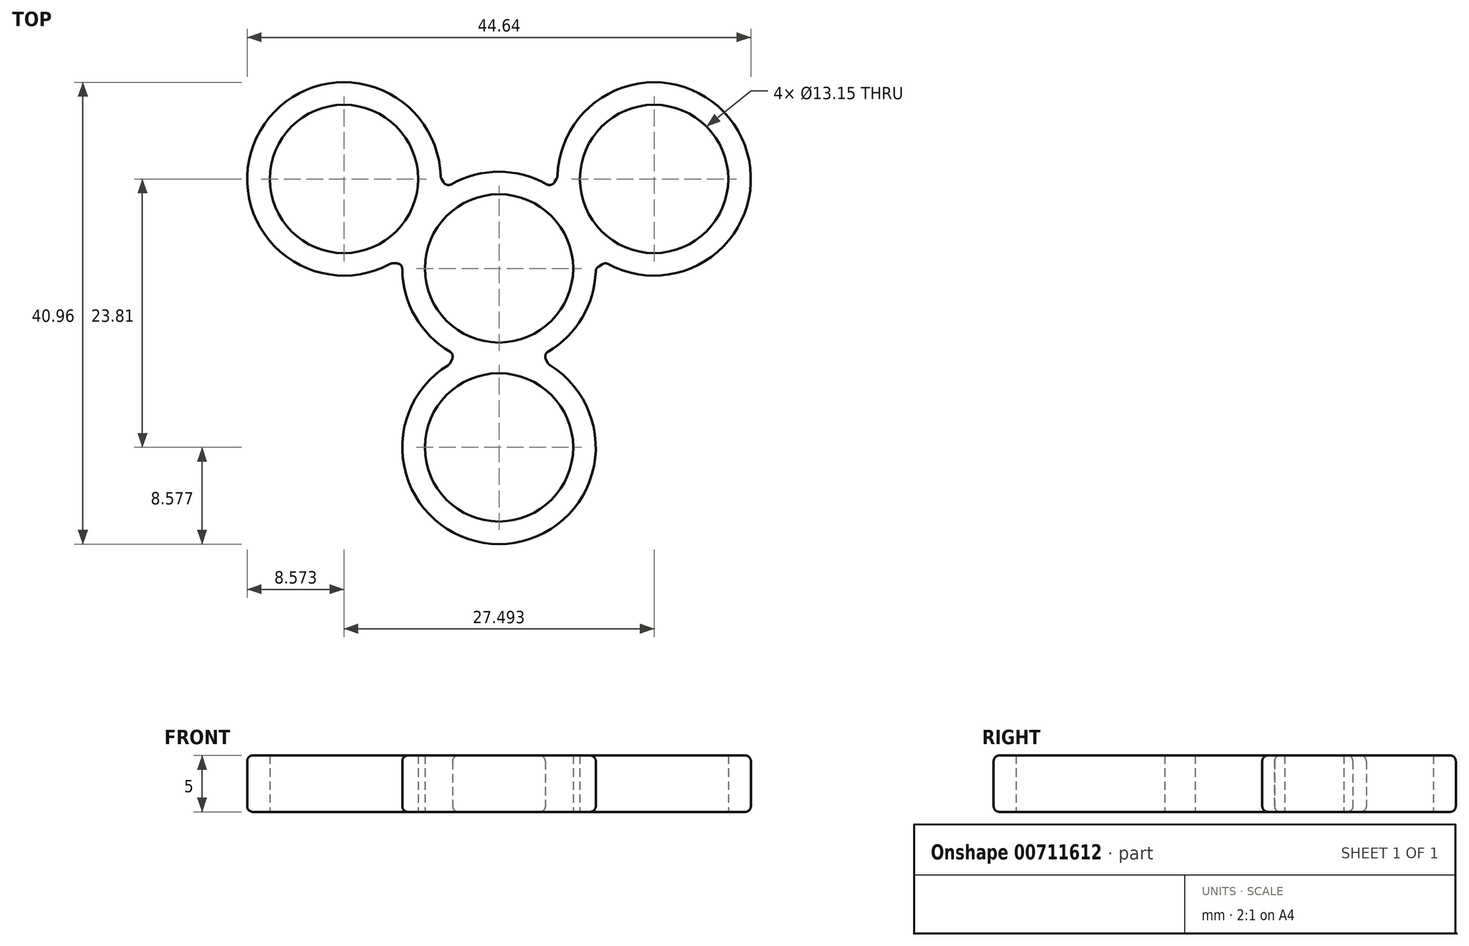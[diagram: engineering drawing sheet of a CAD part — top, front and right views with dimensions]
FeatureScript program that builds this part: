
annotation { "Feature Type Name" : "Feature", "Feature Type Description" : "" }
export const myFeature = defineFeature(function(context is Context, id is Id, definition is map)
    precondition{}
    {
        {
            assignVariable(context, id + "F0", {"name" : "bearing_thickness", "anyValue" : 5});
        }
        {
            var Q0;
            Q0=qCreatedBy(makeId("Top.planeOp"),FACE);
            var sketch = newSketch(context, id + "F1", { "sketchPlane" : qUnion([Q0])});
            skCircle(sketch, "E0", {"center": v(-13.75, 7.94) * mm, "radius": 6.57 * mm});
            skCircle(sketch, "E1", {"center": v(13.75, 7.94) * mm, "radius": 6.58 * mm});
            skCircle(sketch, "E2", {"center": v(0, -15.87) * mm, "radius": 6.58 * mm});
            skCircle(sketch, "E3", {"center": v(0, 0) * mm, "radius": 6.58 * mm});
            skLineSegment(sketch, "E4", {"start": v(-13.75, 7.94) * mm, "end": v(13.75, 7.94) * mm, "construction": true});
            skLineSegment(sketch, "E5", {"start": v(-13.75, 7.94) * mm, "end": v(0, -15.87) * mm, "construction": true});
            skLineSegment(sketch, "E6", {"start": v(13.75, 7.94) * mm, "end": v(0, -15.87) * mm, "construction": true});
            skLineSegment(sketch, "E7", {"start": v(0, 0) * mm, "end": v(-13.75, 7.94) * mm, "construction": true});
            skLineSegment(sketch, "E8", {"start": v(0, 0) * mm, "end": v(13.75, 7.94) * mm, "construction": true});
            skLineSegment(sketch, "E9", {"start": v(0, 0) * mm, "end": v(0, -15.87) * mm, "construction": true});
            skArc(sketch, "E10", {"start": v(-5.17, 8.06) * mm, "mid": v(-21.17, 12.22) * mm, "end": v(-9.56, 0.45) * mm});
            skArc(sketch, "E11", {"start": v(5.17, 8.06) * mm, "mid": v(21.21, 12.15) * mm, "end": v(9.42, 0.53) * mm});
            skArc(sketch, "E12", {"start": v(-4.4, -8.5) * mm, "mid": v(0, -24.45) * mm, "end": v(4.4, -8.5) * mm});
            skCircle(sketch, "E13", {"center": v(0, 0) * mm, "radius": 8.57 * mm});
            skLineSegment(sketch, "E14", {"start": v(-5.17, 8.06) * mm, "end": v(-4.63, 7.22) * mm});
            skLineSegment(sketch, "E15", {"start": v(-9.56, 0.45) * mm, "end": v(-8.56, 0.45) * mm});
            skLineSegment(sketch, "E16", {"start": v(5.17, 8.06) * mm, "end": v(4.63, 7.22) * mm});
            skLineSegment(sketch, "E17", {"start": v(9.42, 0.53) * mm, "end": v(8.57, 0) * mm});
            skLineSegment(sketch, "E18", {"start": v(4.4, -8.5) * mm, "end": v(3.93, -7.62) * mm});
            skLineSegment(sketch, "E19", {"start": v(-4.4, -8.5) * mm, "end": v(-3.93, -7.62) * mm});
            skSolve(sketch);
        }
        {
            var Q0;
            Q0=makeQuery(id+"F1.imprint","IMPRINT",FACE,{"disambiguationData":[TD([[makeQuery(id+"F1.imprint","IMPRINT",EDGE,{"derivedFrom":sQuery(id+"F1.wireOp",EDGE,"E0")}),-1.0]])]});
            var Q1;
            Q1=makeQuery(id+"F1.imprint","IMPRINT",FACE,{"disambiguationData":[TD([[makeQuery(id+"F1.imprint","IMPRINT",EDGE,{"derivedFrom":sQuery(id+"F1.wireOp",EDGE,"E1")}),-1.0]])]});
            var Q2;
            Q2=makeQuery(id+"F1.imprint","IMPRINT",FACE,{"disambiguationData":[TD([[makeQuery(id+"F1.imprint","IMPRINT",EDGE,{"derivedFrom":sQuery(id+"F1.wireOp",EDGE,"E2")}),-1.0]])]});
            var Q3;
            Q3=makeQuery(id+"F1.imprint","IMPRINT",FACE,{"disambiguationData":[TD([[makeQuery(id+"F1.imprint","IMPRINT",EDGE,{"derivedFrom":sQuery(id+"F1.wireOp",EDGE,"E3")}),-1.0]])]});
            extrude(context, id + "F2", {"entities" : qUnion([Q0, Q1, Q2, Q3]), "depth" : (getVariable(context, 'bearing_thickness')) * mm, "offsetDistance" : 25 * mm});
        }
        {
            var Q0;
            Q0=makeQuery(id+"F2.opExtrude","SWEPT_FACE",FACE,{"disambiguationData":[OSD([sQuery(id+"F1.wireOp",EDGE,"E10")])]});
            var Q1;
            {var subQ0=sQuery(id+"F1.wireOp",EDGE,"E13");Q1=makeQuery(id+"F2.opExtrude","SWEPT_FACE",FACE,{"disambiguationData":[OSD([subQ0]),TDD([makeQuery(id+"F1.imprint","IMPRINT",EDGE,{"disambiguationData":[TD([[makeQuery(id+"F1.imprint","INTERSECT",VERTEX,{"derivedFrom":[subQ0,sQuery(id+"F1.wireOp",EDGE,"E15")]}),-1.0]])],"derivedFrom":subQ0})])]});}
            var Q2;
            Q2=makeQuery(id+"F2.opExtrude","SWEPT_FACE",FACE,{"disambiguationData":[OSD([sQuery(id+"F1.wireOp",EDGE,"E12")])]});
            var Q3;
            Q3=makeQuery(id+"F2.opExtrude","SWEPT_FACE",FACE,{"disambiguationData":[OSD([sQuery(id+"F1.wireOp",EDGE,"E15")])]});
            var Q4;
            Q4=makeQuery(id+"F2.opExtrude","SWEPT_FACE",FACE,{"disambiguationData":[OSD([sQuery(id+"F1.wireOp",EDGE,"E19")])]});
            var Q5;
            Q5=makeQuery(id+"F2.opExtrude","SWEPT_FACE",FACE,{"disambiguationData":[OSD([sQuery(id+"F1.wireOp",EDGE,"E18")])]});
            var Q6;
            {var subQ0=sQuery(id+"F1.wireOp",EDGE,"E13");Q6=makeQuery(id+"F2.opExtrude","SWEPT_FACE",FACE,{"disambiguationData":[OSD([subQ0]),TDD([makeQuery(id+"F1.imprint","IMPRINT",EDGE,{"disambiguationData":[TD([[makeQuery(id+"F1.imprint","INTERSECT",VERTEX,{"derivedFrom":[subQ0,sQuery(id+"F1.wireOp",EDGE,"E17")]}),1.0]])],"derivedFrom":subQ0})])]});}
            var Q7;
            Q7=makeQuery(id+"F2.opExtrude","SWEPT_FACE",FACE,{"disambiguationData":[OSD([sQuery(id+"F1.wireOp",EDGE,"E11")])]});
            var Q8;
            Q8=makeQuery(id+"F2.opExtrude","SWEPT_FACE",FACE,{"disambiguationData":[OSD([sQuery(id+"F1.wireOp",EDGE,"E16")])]});
            var Q9;
            {var subQ0=sQuery(id+"F1.wireOp",EDGE,"E13");Q9=makeQuery(id+"F2.opExtrude","SWEPT_FACE",FACE,{"disambiguationData":[OSD([subQ0]),TDD([makeQuery(id+"F1.imprint","IMPRINT",EDGE,{"disambiguationData":[TD([[makeQuery(id+"F1.imprint","INTERSECT",VERTEX,{"derivedFrom":[subQ0,sQuery(id+"F1.wireOp",EDGE,"E14")]}),1.0]])],"derivedFrom":subQ0})])]});}
            var Q10;
            Q10=makeQuery(id+"F2.opExtrude","SWEPT_FACE",FACE,{"disambiguationData":[OSD([sQuery(id+"F1.wireOp",EDGE,"E14")])]});
            var Q11;
            Q11=makeQuery(id+"F2.opExtrude","SWEPT_FACE",FACE,{"disambiguationData":[OSD([sQuery(id+"F1.wireOp",EDGE,"E17")])]});
            fillet(context, id + "F3", {"entities" : qUnion([Q0, Q1, Q2, Q3, Q4, Q5, Q6, Q7, Q8, Q9, Q10, Q11]), "radius" : .5 * mm, "tangentPropagation" : true, "allowEdgeOverflow" : false});
        }
    });
